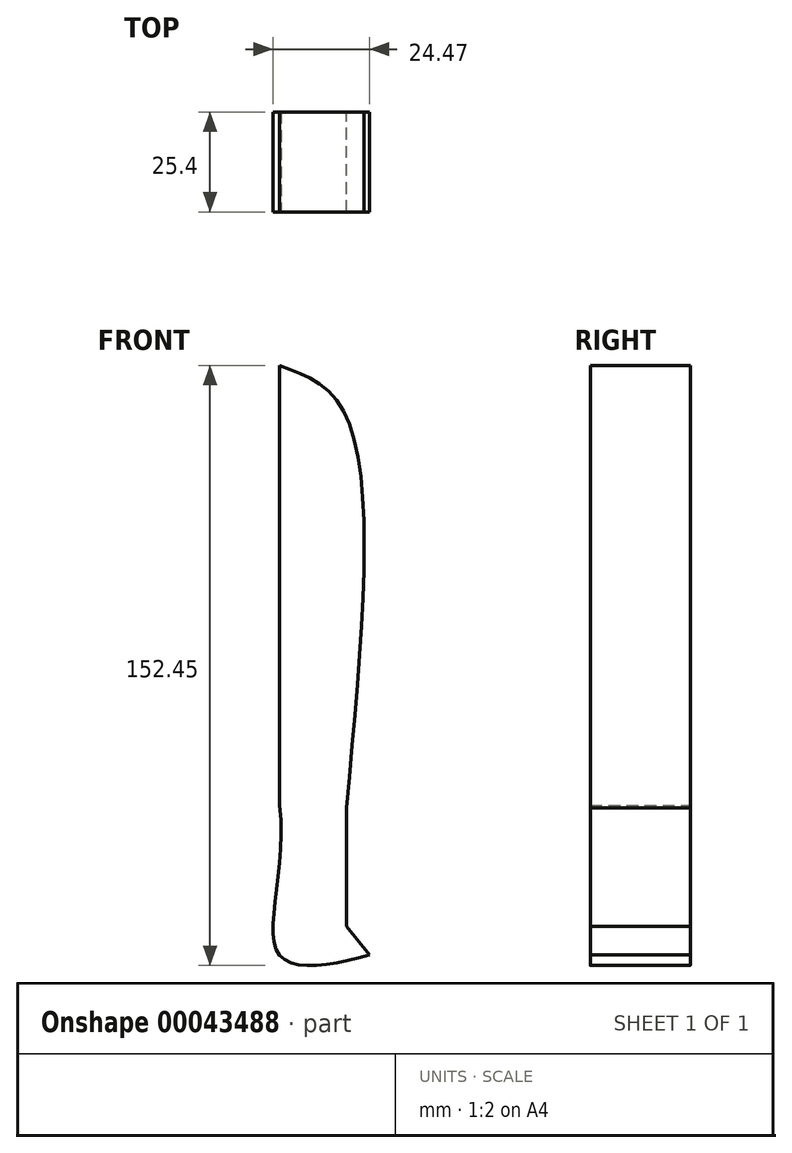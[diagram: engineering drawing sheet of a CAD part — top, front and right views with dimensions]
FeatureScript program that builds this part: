
annotation { "Feature Type Name" : "Feature", "Feature Type Description" : "" }
export const myFeature = defineFeature(function(context is Context, id is Id, definition is map)
    precondition{}
    {
        {
            var Q0;
            Q0=qCreatedBy(makeId("Front.planeOp"),FACE);
            var sketch = newSketch(context, id + "F0", { "sketchPlane" : qUnion([Q0])});
            skFitSpline(sketch, "E0", {"points": [v(16.98, -38.15) * mm, v(16.5, 62.3) * mm, v(0, 74.27) * mm], "startDerivative": vector(17.39, 182.67) * mm, "endDerivative": vector(-61.3, 21.87) * mm});
            skFitSpline(sketch, "E1", {"points": [v(0, 74.27) * mm, v(0, -37.45) * mm, v(0, -42.22) * mm], "startDerivative": vector(0, -179.32) * mm, "endDerivative": vector(0, -16.79) * mm});
            skLineSegment(sketch, "E2", {"start": v(0, -37.45) * mm, "end": v(16.98, -38.15) * mm});
            skLineSegment(sketch, "E3", {"start": v(16.98, -38.15) * mm, "end": v(16.98, -68.29) * mm});
            skLineSegment(sketch, "E4", {"start": v(16.98, -68.29) * mm, "end": v(22.85, -75.49) * mm});
            skFitSpline(sketch, "E5", {"points": [v(22.85, -75.49) * mm, v(0, -75.49) * mm, v(0, -37.45) * mm], "startDerivative": vector(-62.4, -17.97) * mm, "endDerivative": vector(-11.3, 85.8) * mm});
            skSolve(sketch);
        }
        {
            var Q0;
            Q0 = qSketchRegion(id + "F0", true);
            extrude(context, id + "F1", {"entities" : qUnion([Q0]), "depth" : 25.4 * mm});
        }
    });
